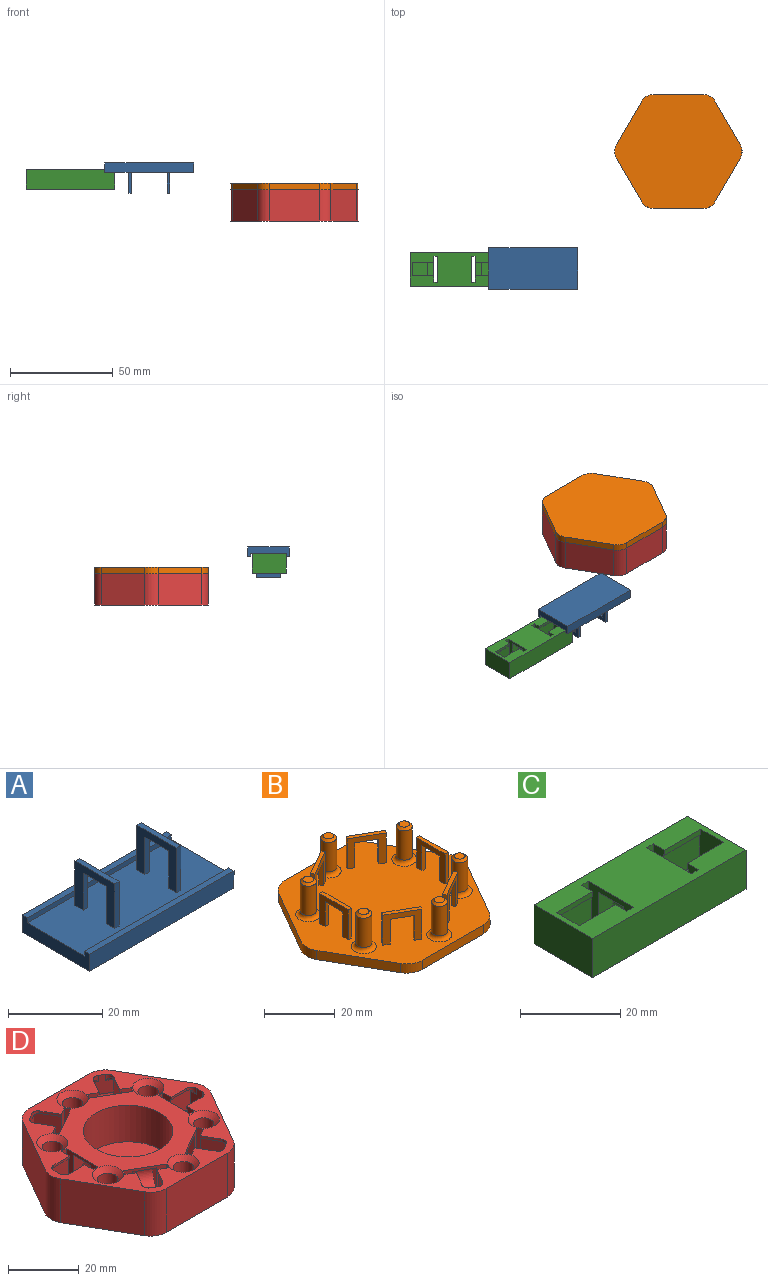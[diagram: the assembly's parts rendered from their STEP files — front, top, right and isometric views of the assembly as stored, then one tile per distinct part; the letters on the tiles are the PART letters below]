
ASSEMBLY  parts=4 mates=3
PART A: 26 faces, bbox 43.2x20.3x14.7 mm
  f0: plane 43.18x17.27mm, normal (0,0,1), area 733.5mm2, adj f1,f5,f8,f9,f10,f12,f13,f15
  f1: plane 20.32x4.45mm, normal (-1,0,0), area 68.4mm2, adj f0,f2,f3,f4,f5,f6,f7,f8
  f2: plane 43.18x4.45mm, normal (0,-1,0), area 191.9mm2, adj f1,f4,f6,f17
  f3: plane 43.18x4.45mm, normal (0,1,0), area 191.9mm2, adj f1,f4,f7,f17
  f4: plane 43.18x20.32mm, normal (0,0,-1), area 877.4mm2, adj f1,f2,f3,f17
  f5: plane 43.18x1.27mm, normal (0,1,0), area 54.8mm2, adj f0,f1,f6,f17
  f6: plane 43.18x1.52mm, normal (0,0,1), area 65.8mm2, adj f1,f2,f5,f17
  f7: plane 43.18x1.52mm, normal (0,0,1), area 65.8mm2, adj f1,f3,f8,f17
  f8: plane 43.18x1.27mm, normal (0,-1,0), area 54.8mm2, adj f0,f1,f7,f17
  f9: plane 11.56x1.27mm, normal (0,-1,0), area 14.7mm2, adj f0,f14,f15,f16
  f10: plane 9.65x1.27mm, normal (0,1,0), area 12.3mm2, adj f0,f11,f15,f16
  f11: plane 7.11x1.27mm, normal (0,0,-1), area 9mm2, adj f10,f12,f15,f16
  f12: plane 9.65x1.27mm, normal (0,-1,0), area 12.3mm2, adj f0,f11,f15,f16
  f13: plane 11.56x1.27mm, normal (0,1,0), area 14.7mm2, adj f0,f14,f15,f16
  f14: plane 11.94x1.27mm, normal (0,0,1), area 15.2mm2, adj f9,f13,f15,f16
  f15: plane 11.94x11.56mm, normal (-1,0,0), area 69.3mm2, adj f0,f9,f10,f11,f12,f13,f14
  f16: plane 11.94x11.56mm, normal (1,0,0), area 69.3mm2, adj f0,f9,f10,f11,f12,f13,f14
  f17: plane 20.32x4.45mm, normal (1,0,0), area 68.4mm2, adj f0,f2,f3,f4,f5,f6,f7,f8
  f18: plane 11.56x1.27mm, normal (0,-1,0), area 14.7mm2, adj f0,f23,f24,f25
  f19: plane 9.65x1.27mm, normal (0,1,0), area 12.3mm2, adj f0,f20,f24,f25
  f20: plane 7.11x1.27mm, normal (0,0,-1), area 9mm2, adj f19,f21,f24,f25
  f21: plane 9.65x1.27mm, normal (0,-1,0), area 12.3mm2, adj f0,f20,f24,f25
  f22: plane 11.56x1.27mm, normal (0,1,0), area 14.7mm2, adj f0,f23,f24,f25
  f23: plane 11.94x1.27mm, normal (0,0,1), area 15.2mm2, adj f18,f22,f24,f25
  f24: plane 11.94x11.56mm, normal (1,0,0), area 69.3mm2, adj f0,f18,f19,f20,f21,f22,f23
  f25: plane 11.94x11.56mm, normal (-1,0,0), area 69.3mm2, adj f0,f18,f19,f20,f21,f22,f23
PART B: 86 faces, bbox 61.8x55.2x15.4 mm
  f0: plane 21.27x12.28mm, normal (0.87,-0.5,0), area 78mm2, adj f6,f7,f80,f85
  f1: plane 21.27x12.28mm, normal (0.87,0.5,0), area 78mm2, adj f6,f7,f80,f81
  f2: plane 24.56x3.18mm, normal (0,1,0), area 78mm2, adj f6,f7,f81,f82
  f3: plane 21.27x12.28mm, normal (-0.87,0.5,0), area 78mm2, adj f6,f7,f82,f83
  f4: plane 21.27x12.28mm, normal (-0.87,-0.5,0), area 78mm2, adj f6,f7,f83,f84
  f5: plane 24.56x3.18mm, normal (0,-1,0), area 78mm2, adj f6,f7,f84,f85
  f6: plane 61.83x55.25mm, normal (0,0,1), area 2358.9mm2, adj f0,f1,f2,f3,f4,f5,f8,f10
  f7: plane 61.83x55.25mm, normal (0,0,-1), area 2630.1mm2, adj f0,f1,f2,f3,f4,f5,f80,f81
  f8: plane 10.41x1.27mm, normal (0,1,0), area 13.2mm2, adj f6,f9,f14,f15
  f9: plane 11.43x1.27mm, normal (0,0,1), area 14.5mm2, adj f8,f10,f14,f15
  f10: plane 10.41x1.27mm, normal (0,-1,0), area 13.2mm2, adj f6,f9,f14,f15
  f11: plane 8.64x1.27mm, normal (0,1,0), area 11mm2, adj f6,f12,f14,f15
  f12: plane 7.11x1.27mm, normal (0,0,-1), area 9mm2, adj f11,f13,f14,f15
  f13: plane 8.64x1.27mm, normal (0,-1,0), area 11mm2, adj f6,f12,f14,f15
  f14: plane 11.43x10.41mm, normal (1,0,0), area 57.6mm2, adj f6,f8,f9,f10,f11,f12,f13
  f15: plane 11.43x10.41mm, normal (-1,0,0), area 57.6mm2, adj f6,f8,f9,f10,f11,f12,f13
  f16: cylinder r=2.29mm len=10.16mm, axis (0,0,-1), area 145.9mm2, adj f18,f19
  f17: plane 3.05x3.05mm, normal (0,0,1), area 7.3mm2, adj f18
  f18: cone r=1.52mm half-angle=45deg, axis (0,0,-1), area 12.9mm2, adj f16,f17
  f19: torus R=3.56mm, axis (0,0,1), area 34.4mm2, adj f6,f16
  f20: plane 10.41x1.1mm, normal (-0.87,0.5,0), area 13.2mm2, adj f6,f21,f26,f27
  f21: plane 10.53x6.82mm, normal (0,0,1), area 14.5mm2, adj f20,f22,f26,f27
  f22: plane 10.41x1.1mm, normal (0.87,-0.5,0), area 13.2mm2, adj f6,f21,f26,f27
  f23: plane 8.64x1.1mm, normal (-0.87,0.5,0), area 11mm2, adj f6,f24,f26,f27
  f24: plane 6.79x4.66mm, normal (0,0,-1), area 9mm2, adj f23,f25,f26,f27
  f25: plane 8.64x1.1mm, normal (0.87,-0.5,0), area 11mm2, adj f6,f24,f26,f27
  f26: plane 10.41x9.9mm, normal (0.5,0.87,0), area 57.6mm2, adj f6,f20,f21,f22,f23,f24,f25
  f27: plane 10.41x9.9mm, normal (-0.5,-0.87,0), area 57.6mm2, adj f6,f20,f21,f22,f23,f24,f25
  f28: cylinder r=2.29mm len=10.16mm, axis (0,0,-1), area 145.9mm2, adj f30,f31
  f29: plane 3.05x3.05mm, normal (0,0,1), area 7.3mm2, adj f30
  f30: cone r=1.52mm half-angle=45deg, axis (0,0,-1), area 12.9mm2, adj f28,f29
  f31: torus R=3.56mm, axis (0,0,1), area 34.4mm2, adj f6,f28
  f32: plane 10.41x1.1mm, normal (-0.87,-0.5,0), area 13.2mm2, adj f6,f33,f38,f39
  f33: plane 10.53x6.82mm, normal (0,0,1), area 14.5mm2, adj f32,f34,f38,f39
  f34: plane 10.41x1.1mm, normal (0.87,0.5,0), area 13.2mm2, adj f6,f33,f38,f39
  f35: plane 8.64x1.1mm, normal (-0.87,-0.5,0), area 11mm2, adj f6,f36,f38,f39
  f36: plane 6.79x4.66mm, normal (0,0,-1), area 9mm2, adj f35,f37,f38,f39
  f37: plane 8.64x1.1mm, normal (0.87,0.5,0), area 11mm2, adj f6,f36,f38,f39
  f38: plane 10.41x9.9mm, normal (-0.5,0.87,0), area 57.6mm2, adj f6,f32,f33,f34,f35,f36,f37
  f39: plane 10.41x9.9mm, normal (0.5,-0.87,0), area 57.6mm2, adj f6,f32,f33,f34,f35,f36,f37
  f40: cylinder r=2.29mm len=10.16mm, axis (0,0,-1), area 145.9mm2, adj f42,f43
  f41: plane 3.05x3.05mm, normal (0,0,1), area 7.3mm2, adj f42
  f42: cone r=1.52mm half-angle=45deg, axis (0,0,-1), area 12.9mm2, adj f40,f41
  f43: torus R=3.56mm, axis (0,0,1), area 34.4mm2, adj f6,f40
  f44: plane 10.41x1.27mm, normal (0,-1,0), area 13.2mm2, adj f6,f45,f50,f51
  f45: plane 11.43x1.27mm, normal (0,0,1), area 14.5mm2, adj f44,f46,f50,f51
  f46: plane 10.41x1.27mm, normal (0,1,0), area 13.2mm2, adj f6,f45,f50,f51
  f47: plane 8.64x1.27mm, normal (0,-1,0), area 11mm2, adj f6,f48,f50,f51
  f48: plane 7.11x1.27mm, normal (0,0,-1), area 9mm2, adj f47,f49,f50,f51
  f49: plane 8.64x1.27mm, normal (0,1,0), area 11mm2, adj f6,f48,f50,f51
  f50: plane 11.43x10.41mm, normal (-1,0,0), area 57.6mm2, adj f6,f44,f45,f46,f47,f48,f49
  f51: plane 11.43x10.41mm, normal (1,0,0), area 57.6mm2, adj f6,f44,f45,f46,f47,f48,f49
  f52: cylinder r=2.29mm len=10.16mm, axis (0,0,-1), area 145.9mm2, adj f54,f55
  f53: plane 3.05x3.05mm, normal (0,0,1), area 7.3mm2, adj f54
  f54: cone r=1.52mm half-angle=45deg, axis (0,0,-1), area 12.9mm2, adj f52,f53
  f55: torus R=3.56mm, axis (0,0,1), area 34.4mm2, adj f6,f52
  f56: plane 10.41x1.1mm, normal (0.87,-0.5,0), area 13.2mm2, adj f6,f57,f62,f63
  f57: plane 10.53x6.82mm, normal (0,0,1), area 14.5mm2, adj f56,f58,f62,f63
  f58: plane 10.41x1.1mm, normal (-0.87,0.5,0), area 13.2mm2, adj f6,f57,f62,f63
  f59: plane 8.64x1.1mm, normal (0.87,-0.5,0), area 11mm2, adj f6,f60,f62,f63
  f60: plane 6.79x4.66mm, normal (0,0,-1), area 9mm2, adj f59,f61,f62,f63
  f61: plane 8.64x1.1mm, normal (-0.87,0.5,0), area 11mm2, adj f6,f60,f62,f63
  f62: plane 10.41x9.9mm, normal (-0.5,-0.87,0), area 57.6mm2, adj f6,f56,f57,f58,f59,f60,f61
  f63: plane 10.41x9.9mm, normal (0.5,0.87,0), area 57.6mm2, adj f6,f56,f57,f58,f59,f60,f61
  f64: cylinder r=2.29mm len=10.16mm, axis (0,0,-1), area 145.9mm2, adj f66,f67
  f65: plane 3.05x3.05mm, normal (0,0,1), area 7.3mm2, adj f66
  f66: cone r=1.52mm half-angle=45deg, axis (0,0,-1), area 12.9mm2, adj f64,f65
  f67: torus R=3.56mm, axis (0,0,1), area 34.4mm2, adj f6,f64
  f68: plane 10.41x1.1mm, normal (0.87,0.5,0), area 13.2mm2, adj f6,f69,f74,f75
  f69: plane 10.53x6.82mm, normal (0,0,1), area 14.5mm2, adj f68,f70,f74,f75
  f70: plane 10.41x1.1mm, normal (-0.87,-0.5,0), area 13.2mm2, adj f6,f69,f74,f75
  f71: plane 8.64x1.1mm, normal (0.87,0.5,0), area 11mm2, adj f6,f72,f74,f75
  f72: plane 6.79x4.66mm, normal (0,0,-1), area 9mm2, adj f71,f73,f74,f75
  f73: plane 8.64x1.1mm, normal (-0.87,-0.5,0), area 11mm2, adj f6,f72,f74,f75
  f74: plane 10.41x9.9mm, normal (0.5,-0.87,0), area 57.6mm2, adj f6,f68,f69,f70,f71,f72,f73
  f75: plane 10.41x9.9mm, normal (-0.5,0.87,0), area 57.6mm2, adj f6,f68,f69,f70,f71,f72,f73
  f76: cylinder r=2.29mm len=10.16mm, axis (0,0,-1), area 145.9mm2, adj f78,f79
  f77: plane 3.05x3.05mm, normal (0,0,1), area 7.3mm2, adj f78
  f78: cone r=1.52mm half-angle=45deg, axis (0,0,-1), area 12.9mm2, adj f76,f77
  f79: torus R=3.56mm, axis (0,0,1), area 34.4mm2, adj f6,f76
  f80: cylinder r=6.35mm len=6.35mm, axis (0,0,-1), area 21.1mm2, adj f0,f1,f6,f7
  f81: cylinder r=6.35mm len=5.5mm, axis (0,0,-1), area 21.1mm2, adj f1,f2,f6,f7
  f82: cylinder r=6.35mm len=5.5mm, axis (0,0,-1), area 21.1mm2, adj f2,f3,f6,f7
  f83: cylinder r=6.35mm len=6.35mm, axis (0,0,-1), area 21.1mm2, adj f3,f4,f6,f7
  f84: cylinder r=6.35mm len=5.5mm, axis (0,0,-1), area 21.1mm2, adj f4,f5,f6,f7
  f85: cylinder r=6.35mm len=5.5mm, axis (0,0,-1), area 21.1mm2, adj f0,f5,f6,f7
PART C: 52 faces, bbox 43.2x16.5x9.5 mm
  f0: plane 6.99x0.38mm, normal (0.02,0,-1), area 2.7mm2, adj f1,f6,f13,f26
  f1: cylinder r=10.16mm len=0.53mm, axis (0,1,0), area 0.2mm2, adj f0,f2,f13,f26
  f2: plane 2.74x0.38mm, normal (-0.03,0,-1), area 1mm2, adj f1,f3,f13,f26
  f3: plane 12.7x9.53mm, normal (1,0,0), area 63.3mm2, adj f2,f4,f9,f10,f12,f13,f14,f15
  f4: plane 43.18x16.51mm, normal (0,0,1), area 534.2mm2, adj f3,f6,f14,f15,f16,f18,f19,f20
  f5: plane 7.11x7.11mm, normal (-0.02,0,1), area 50.6mm2, adj f6,f11,f12,f13
  f6: plane 8.26x7.11mm, normal (1,0,0), area 57.7mm2, adj f0,f4,f5,f7,f12,f13,f26,f27
  f7: plane 6.99x0.38mm, normal (0.02,0,-1), area 2.7mm2, adj f6,f8,f12,f27
  f8: cylinder r=10.16mm len=0.53mm, axis (0,1,0), area 0.2mm2, adj f7,f9,f12,f27
  f9: plane 2.74x0.38mm, normal (-0.03,0,-1), area 1mm2, adj f3,f8,f12,f27
  f10: plane 7.11x2.98mm, normal (0.03,0,1), area 21.2mm2, adj f3,f11,f12,f13
  f11: cylinder r=3.17mm len=7.11mm, axis (0,1,0), area 1.2mm2, adj f5,f10,f12,f13
  f12: plane 10.26x7.11mm, normal (0,1,0), area 71.7mm2, adj f3,f5,f6,f7,f8,f9,f10,f11
  f13: plane 10.26x7.11mm, normal (0,-1,0), area 71.7mm2, adj f0,f1,f2,f3,f5,f6,f10,f11
  f14: plane 9.53x1.91mm, normal (0,-1,0), area 18.1mm2, adj f3,f4,f16,f17
  f15: plane 9.53x1.91mm, normal (0,1,0), area 18.1mm2, adj f3,f4,f16,f17
  f16: plane 12.7x9.53mm, normal (-1,0,0), area 71.3mm2, adj f4,f14,f15,f17,f22,f23,f24,f25
  f17: plane 43.18x16.51mm, normal (0,0,-1), area 664.5mm2, adj f3,f14,f15,f16,f18,f19,f20,f31
  f18: plane 16.51x9.53mm, normal (-1,0,0), area 157.3mm2, adj f4,f17,f19,f20
  f19: plane 43.18x9.53mm, normal (0,-1,0), area 411.3mm2, adj f4,f17,f18,f44
  f20: plane 43.18x9.53mm, normal (0,1,0), area 411.3mm2, adj f4,f17,f18,f44
  f21: cylinder r=3.49mm len=7.11mm, axis (0,1,0), area 78mm2, adj f22,f23,f24,f25
  f22: plane 7.02x4.32mm, normal (0,1,0), area 24.9mm2, adj f16,f21,f24,f25
  f23: plane 7.02x4.32mm, normal (0,-1,0), area 24.9mm2, adj f16,f21,f24,f25
  f24: plane 7.11x0.71mm, normal (0.03,0,1), area 5mm2, adj f16,f21,f22,f23
  f25: plane 7.11x0.95mm, normal (-0.03,0,-1), area 6.8mm2, adj f16,f21,f22,f23
  f26: plane 10.26x1.27mm, normal (0,-1,0), area 12.3mm2, adj f0,f1,f2,f3,f4,f6
  f27: plane 10.26x1.27mm, normal (0,1,0), area 12.3mm2, adj f3,f4,f6,f7,f8,f9
  f28: plane 6.99x0.38mm, normal (-0.02,0,-1), area 2.7mm2, adj f29,f33,f40,f50
  f29: cylinder r=10.16mm len=0.53mm, axis (0,1,0), area 0.2mm2, adj f28,f30,f40,f50
  f30: plane 2.74x0.38mm, normal (0.03,0,-1), area 1mm2, adj f29,f31,f40,f50
  f31: plane 12.7x9.53mm, normal (-1,0,0), area 63.3mm2, adj f4,f17,f30,f36,f37,f39,f40,f41
  f32: plane 7.11x7.11mm, normal (0.02,0,1), area 50.6mm2, adj f33,f38,f39,f40
  f33: plane 8.26x7.11mm, normal (-1,0,0), area 57.7mm2, adj f4,f28,f32,f34,f39,f40,f50,f51
  f34: plane 6.99x0.38mm, normal (-0.02,0,-1), area 2.7mm2, adj f33,f35,f39,f51
  f35: cylinder r=10.16mm len=0.53mm, axis (0,1,0), area 0.2mm2, adj f34,f36,f39,f51
  f36: plane 2.74x0.38mm, normal (0.03,0,-1), area 1mm2, adj f31,f35,f39,f51
  f37: plane 7.11x2.98mm, normal (-0.03,0,1), area 21.2mm2, adj f31,f38,f39,f40
  f38: cylinder r=3.17mm len=7.11mm, axis (0,1,0), area 1.2mm2, adj f32,f37,f39,f40
  f39: plane 10.26x7.11mm, normal (0,1,0), area 71.7mm2, adj f31,f32,f33,f34,f35,f36,f37,f38
  f40: plane 10.26x7.11mm, normal (0,-1,0), area 71.7mm2, adj f28,f29,f30,f31,f32,f33,f37,f38
  f41: plane 9.53x1.91mm, normal (0,-1,0), area 18.1mm2, adj f4,f17,f31,f43
  f42: plane 9.53x1.91mm, normal (0,1,0), area 18.1mm2, adj f4,f17,f31,f43
  f43: plane 12.7x9.53mm, normal (1,0,0), area 71.3mm2, adj f4,f17,f41,f42,f46,f47,f48,f49
  f44: plane 16.51x9.53mm, normal (1,0,0), area 157.3mm2, adj f4,f17,f19,f20
  f45: cylinder r=3.49mm len=7.11mm, axis (0,1,0), area 78mm2, adj f46,f47,f48,f49
  f46: plane 7.02x4.32mm, normal (0,1,0), area 24.9mm2, adj f43,f45,f48,f49
  f47: plane 7.02x4.32mm, normal (0,-1,0), area 24.9mm2, adj f43,f45,f48,f49
  f48: plane 7.11x0.71mm, normal (-0.03,0,1), area 5mm2, adj f43,f45,f46,f47
  f49: plane 7.11x0.95mm, normal (0.03,0,-1), area 6.8mm2, adj f43,f45,f46,f47
  f50: plane 10.26x1.27mm, normal (0,-1,0), area 12.3mm2, adj f4,f28,f29,f30,f31,f33
  f51: plane 10.26x1.27mm, normal (0,1,0), area 12.3mm2, adj f4,f31,f33,f34,f35,f36
PART D: 196 faces, bbox 61.8x55.2x15.2 mm
  f0: plane 61.83x55.25mm, normal (0,0,1), area 1314.2mm2, adj f1,f5,f9,f13,f17,f24,f32,f35
  f1: plane 11x10.92mm, normal (0.5,0.87,0), area 85mm2, adj f0,f2,f159,f161,f162,f163,f164,f165
  f2: plane 1.85x1.32mm, normal (-0.01,-0.02,-1), area 0.8mm2, adj f1,f3,f165,f178
  f3: plane 4.71x2.94mm, normal (0.01,0.02,-1), area 2.3mm2, adj f2,f4,f165,f178,f180
  f4: cylinder r=1.27mm len=2.65mm, axis (0.87,-0.5,0), area 2.6mm2, adj f3,f165,f170,f180
  f5: plane 11x10.92mm, normal (-0.5,0.87,0), area 85mm2, adj f0,f6,f134,f136,f137,f138,f139,f140
  f6: plane 1.85x1.32mm, normal (0.01,-0.02,-1), area 0.8mm2, adj f5,f7,f140,f153
  f7: plane 4.65x3.05mm, normal (-0.01,0.02,-1), area 2.3mm2, adj f6,f8,f140,f153,f155
  f8: cylinder r=1.27mm len=2.65mm, axis (0.87,0.5,0), area 2.6mm2, adj f7,f140,f145,f155
  f9: plane 12.7x10.92mm, normal (-1,0,0), area 85mm2, adj f0,f10,f109,f111,f112,f113,f114,f115
  f10: plane 1.88x0.44mm, normal (0.03,0,-1), area 0.8mm2, adj f9,f11,f115,f128
  f11: plane 5.11x0.57mm, normal (-0.03,0,-1), area 2.3mm2, adj f10,f12,f115,f128,f130
  f12: cylinder r=1.27mm len=2.35mm, axis (0,1,0), area 2.6mm2, adj f11,f115,f120,f130
  f13: plane 11x10.92mm, normal (-0.5,-0.87,0), area 85mm2, adj f0,f14,f84,f86,f87,f88,f89,f90
  f14: plane 1.85x1.32mm, normal (0.01,0.02,-1), area 0.8mm2, adj f13,f15,f90,f103
  f15: plane 4.71x2.94mm, normal (-0.01,-0.02,-1), area 2.3mm2, adj f14,f16,f90,f103,f105
  f16: cylinder r=1.27mm len=2.65mm, axis (-0.87,0.5,0), area 2.6mm2, adj f15,f90,f95,f105
  f17: plane 11x10.92mm, normal (0.5,-0.87,0), area 85mm2, adj f0,f18,f59,f61,f62,f63,f64,f65
  f18: plane 1.85x1.32mm, normal (-0.01,0.02,-1), area 0.8mm2, adj f17,f19,f65,f78
  f19: plane 4.65x3.05mm, normal (0.01,-0.02,-1), area 2.3mm2, adj f18,f20,f65,f78,f80
  f20: cylinder r=1.27mm len=2.65mm, axis (-0.87,-0.5,0), area 2.6mm2, adj f19,f65,f70,f80
  f21: plane 1.88x0.44mm, normal (-0.03,0,-1), area 0.8mm2, adj f22,f24,f27,f53
  f22: plane 5.11x0.57mm, normal (0.03,0,-1), area 2.3mm2, adj f21,f23,f27,f53,f55
  f23: cylinder r=1.27mm len=2.35mm, axis (0,-1,0), area 2.6mm2, adj f22,f27,f32,f55
  f24: plane 12.7x10.92mm, normal (1,0,0), area 85mm2, adj f0,f21,f25,f26,f27,f28,f35,f37
  f25: plane 6.99x1.71mm, normal (0.03,0,1), area 12mm2, adj f24,f27,f28,f29
  f26: plane 1.88x0.44mm, normal (-0.03,0,-1), area 0.8mm2, adj f24,f28,f30,f54
  f27: plane 8.23x7.12mm, normal (0,-1,0), area 56.8mm2, adj f21,f22,f23,f24,f25,f29,f32,f33
  f28: plane 8.23x7.12mm, normal (0,1,0), area 56.8mm2, adj f24,f25,f26,f29,f30,f31,f32,f33
  f29: cylinder r=3.17mm len=6.99mm, axis (0,-1,0), area 1.2mm2, adj f25,f27,f28,f34
  f30: plane 5.11x0.57mm, normal (0.03,0,-1), area 2.3mm2, adj f26,f28,f31,f54,f56
  f31: cylinder r=1.27mm len=2.35mm, axis (0,-1,0), area 2.6mm2, adj f28,f30,f32,f56
  f32: plane 6.99x6.62mm, normal (1,0,0), area 36mm2, adj f0,f23,f27,f28,f31,f33,f55,f56
  f33: cylinder r=1.27mm len=6.99mm, axis (0,-1,0), area 14.2mm2, adj f27,f28,f32,f34
  f34: plane 6.99x5.05mm, normal (-0.03,0,1), area 35.3mm2, adj f27,f28,f29,f33
  f35: plane 10.92x1.91mm, normal (0,1,0), area 20.8mm2, adj f0,f24,f36,f38
  f36: plane 12.7x10.92mm, normal (-1,0,0), area 89.9mm2, adj f0,f35,f37,f38,f49,f50,f51,f52
  f37: plane 10.92x1.91mm, normal (0,-1,0), area 20.8mm2, adj f0,f24,f36,f38
  f38: plane 12.7x1.91mm, normal (0,0,1), area 24.2mm2, adj f24,f35,f36,f37
  f39: plane 21.27x15.24mm, normal (-0.87,-0.5,0), area 374.3mm2, adj f0,f45,f184,f189
  f40: plane 24.56x15.24mm, normal (0,-1,0), area 374.3mm2, adj f0,f45,f184,f185
  f41: plane 21.27x15.24mm, normal (0.87,-0.5,0), area 374.3mm2, adj f0,f45,f185,f186
  f42: plane 21.27x15.24mm, normal (0.87,0.5,0), area 374.3mm2, adj f0,f45,f186,f187
  f43: plane 24.56x15.24mm, normal (0,1,0), area 374.3mm2, adj f0,f45,f187,f188
  f44: plane 21.27x15.24mm, normal (-0.87,0.5,0), area 374.3mm2, adj f0,f45,f188,f189
  f45: plane 61.83x55.25mm, normal (0,0,-1), area 2630.1mm2, adj f39,f40,f41,f42,f43,f44,f184,f185
  f46: cylinder r=12.7mm len=25.4mm, axis (0,0,1), area 1013.4mm2, adj f0,f47
  f47: plane 25.4x25.4mm, normal (0,0,1), area 506.7mm2, adj f46
  f48: cylinder r=3.49mm len=6.99mm, axis (0,-1,0), area 76.6mm2, adj f49,f50,f51,f52
  f49: plane 7.01x4.32mm, normal (0,-1,0), area 24.9mm2, adj f36,f48,f51,f52
  f50: plane 7.01x4.32mm, normal (0,1,0), area 24.9mm2, adj f36,f48,f51,f52
  f51: plane 6.99x0.92mm, normal (-0.03,0,-1), area 6.4mm2, adj f36,f48,f49,f50
  f52: plane 6.99x0.74mm, normal (0.03,0,1), area 5.1mm2, adj f36,f48,f49,f50
  f53: plane 6.32x0.88mm, normal (0,-1,0), area 5.1mm2, adj f0,f21,f22,f24,f55
  f54: plane 6.32x0.88mm, normal (0,1,0), area 5.1mm2, adj f0,f24,f26,f30,f56
  f55: cylinder r=1.91mm len=2.17mm, axis (0,0,1), area 3.8mm2, adj f0,f22,f23,f32,f53
  f56: cylinder r=1.91mm len=2.17mm, axis (0,0,1), area 3.8mm2, adj f0,f30,f31,f32,f54
  f57: cylinder r=2.92mm len=11.18mm, axis (0,0,1), area 205.1mm2, adj f58,f195
  f58: plane 5.84x5.84mm, normal (0,0,1), area 26.8mm2, adj f57
  f59: plane 10.92x1.65mm, normal (0.87,0.5,0), area 20.8mm2, adj f0,f17,f60,f62
  f60: plane 11x10.92mm, normal (-0.5,0.87,0), area 89.9mm2, adj f0,f59,f61,f62,f74,f75,f76,f77
  f61: plane 10.92x1.65mm, normal (-0.87,-0.5,0), area 20.8mm2, adj f0,f17,f60,f62
  f62: plane 11.95x8mm, normal (0,0,1), area 24.2mm2, adj f17,f59,f60,f61
  f63: plane 6.91x4.98mm, normal (0.01,-0.02,1), area 12mm2, adj f17,f65,f66,f67
  f64: plane 1.85x1.32mm, normal (-0.01,0.02,-1), area 0.8mm2, adj f17,f66,f68,f79
  f65: plane 7.13x7.12mm, normal (-0.87,-0.5,0), area 56.8mm2, adj f17,f18,f19,f20,f63,f67,f70,f71
  f66: plane 7.13x7.12mm, normal (0.87,0.5,0), area 56.8mm2, adj f17,f63,f64,f67,f68,f69,f70,f71
  f67: cylinder r=3.17mm len=6.13mm, axis (-0.87,-0.5,0), area 1.2mm2, adj f63,f65,f66,f72
  f68: plane 4.71x2.94mm, normal (0.01,-0.02,-1), area 2.3mm2, adj f64,f66,f69,f79,f81
  f69: cylinder r=1.27mm len=2.65mm, axis (-0.87,-0.5,0), area 2.6mm2, adj f66,f68,f70,f81
  f70: plane 6.62x6.05mm, normal (0.5,-0.87,0), area 36mm2, adj f0,f20,f65,f66,f69,f71,f80,f81
  f71: cylinder r=1.27mm len=6.7mm, axis (-0.87,-0.5,0), area 14.2mm2, adj f65,f66,f70,f72
  f72: plane 8.57x7.86mm, normal (-0.01,0.02,1), area 35.3mm2, adj f65,f66,f67,f71
  f73: cylinder r=3.49mm len=7.84mm, axis (-0.87,-0.5,0), area 76.6mm2, adj f74,f75,f76,f77
  f74: plane 7.01x3.74mm, normal (-0.87,-0.5,0), area 24.9mm2, adj f60,f73,f76,f77
  f75: plane 7.01x3.74mm, normal (0.87,0.5,0), area 24.9mm2, adj f60,f73,f76,f77
  f76: plane 6.51x4.29mm, normal (-0.01,0.02,-1), area 6.4mm2, adj f60,f73,f74,f75
  f77: plane 6.42x4.13mm, normal (0.01,-0.02,1), area 5.1mm2, adj f60,f73,f74,f75
  f78: plane 5.48x3.16mm, normal (-0.87,-0.5,0), area 5.1mm2, adj f0,f17,f18,f19,f80
  f79: plane 5.48x3.16mm, normal (0.87,0.5,0), area 5.1mm2, adj f0,f17,f64,f68,f81
  f80: cylinder r=1.91mm len=2.6mm, axis (0,0,1), area 3.8mm2, adj f0,f19,f20,f70,f78
  f81: cylinder r=1.91mm len=2.6mm, axis (0,0,1), area 3.8mm2, adj f0,f68,f69,f70,f79
  f82: cylinder r=2.92mm len=11.18mm, axis (0,0,1), area 205.1mm2, adj f83,f194
  f83: plane 5.84x5.84mm, normal (0,0,1), area 26.8mm2, adj f82
  f84: plane 10.92x1.65mm, normal (0.87,-0.5,0), area 20.8mm2, adj f0,f13,f85,f87
  f85: plane 11x10.92mm, normal (0.5,0.87,0), area 89.9mm2, adj f0,f84,f86,f87,f99,f100,f101,f102
  f86: plane 10.92x1.65mm, normal (-0.87,0.5,0), area 20.8mm2, adj f0,f13,f85,f87
  f87: plane 11.95x8mm, normal (0,0,1), area 24.2mm2, adj f13,f84,f85,f86
  f88: plane 6.91x4.98mm, normal (-0.01,-0.02,1), area 12mm2, adj f13,f90,f91,f92
  f89: plane 1.85x1.32mm, normal (0.01,0.02,-1), area 0.8mm2, adj f13,f91,f93,f104
  f90: plane 7.13x7.12mm, normal (-0.87,0.5,0), area 56.8mm2, adj f13,f14,f15,f16,f88,f92,f95,f96
  f91: plane 7.13x7.12mm, normal (0.87,-0.5,0), area 56.8mm2, adj f13,f88,f89,f92,f93,f94,f95,f96
  f92: cylinder r=3.17mm len=6.13mm, axis (-0.87,0.5,0), area 1.2mm2, adj f88,f90,f91,f97
  f93: plane 4.65x3.05mm, normal (-0.01,-0.02,-1), area 2.3mm2, adj f89,f91,f94,f104,f106
  f94: cylinder r=1.27mm len=2.65mm, axis (-0.87,0.5,0), area 2.6mm2, adj f91,f93,f95,f106
  f95: plane 6.62x6.05mm, normal (-0.5,-0.87,0), area 36mm2, adj f0,f16,f90,f91,f94,f96,f105,f106
  f96: cylinder r=1.27mm len=6.7mm, axis (-0.87,0.5,0), area 14.2mm2, adj f90,f91,f95,f97
  f97: plane 8.57x7.86mm, normal (0.01,0.02,1), area 35.3mm2, adj f90,f91,f92,f96
  f98: cylinder r=3.49mm len=7.84mm, axis (-0.87,0.5,0), area 76.6mm2, adj f99,f100,f101,f102
  f99: plane 7.01x3.74mm, normal (-0.87,0.5,0), area 24.9mm2, adj f85,f98,f101,f102
  f100: plane 7.01x3.74mm, normal (0.87,-0.5,0), area 24.9mm2, adj f85,f98,f101,f102
  f101: plane 6.51x4.29mm, normal (0.01,0.02,-1), area 6.4mm2, adj f85,f98,f99,f100
  f102: plane 6.42x4.13mm, normal (-0.01,-0.02,1), area 5.1mm2, adj f85,f98,f99,f100
  f103: plane 5.48x3.16mm, normal (-0.87,0.5,0), area 5.1mm2, adj f0,f13,f14,f15,f105
  f104: plane 5.48x3.16mm, normal (0.87,-0.5,0), area 5.1mm2, adj f0,f13,f89,f93,f106
  f105: cylinder r=1.91mm len=2.6mm, axis (0,0,1), area 3.8mm2, adj f0,f15,f16,f95,f103
  f106: cylinder r=1.91mm len=2.6mm, axis (0,0,1), area 3.8mm2, adj f0,f93,f94,f95,f104
  f107: cylinder r=2.92mm len=11.18mm, axis (0,0,1), area 205.1mm2, adj f108,f193
  f108: plane 5.84x5.84mm, normal (0,0,1), area 26.8mm2, adj f107
  f109: plane 10.92x1.91mm, normal (0,-1,0), area 20.8mm2, adj f0,f9,f110,f112
  f110: plane 12.7x10.92mm, normal (1,0,0), area 89.9mm2, adj f0,f109,f111,f112,f124,f125,f126,f127
  f111: plane 10.92x1.91mm, normal (0,1,0), area 20.8mm2, adj f0,f9,f110,f112
  f112: plane 12.7x1.91mm, normal (0,0,1), area 24.2mm2, adj f9,f109,f110,f111
  f113: plane 6.99x1.71mm, normal (-0.03,0,1), area 12mm2, adj f9,f115,f116,f117
  f114: plane 1.88x0.44mm, normal (0.03,0,-1), area 0.8mm2, adj f9,f116,f118,f129
  f115: plane 8.23x7.12mm, normal (0,1,0), area 56.8mm2, adj f9,f10,f11,f12,f113,f117,f120,f121
  f116: plane 8.23x7.12mm, normal (0,-1,0), area 56.8mm2, adj f9,f113,f114,f117,f118,f119,f120,f121
  f117: cylinder r=3.17mm len=6.99mm, axis (0,1,0), area 1.2mm2, adj f113,f115,f116,f122
  f118: plane 5.11x0.57mm, normal (-0.03,0,-1), area 2.3mm2, adj f114,f116,f119,f129,f131
  f119: cylinder r=1.27mm len=2.35mm, axis (0,1,0), area 2.6mm2, adj f116,f118,f120,f131
  f120: plane 6.99x6.62mm, normal (-1,0,0), area 36mm2, adj f0,f12,f115,f116,f119,f121,f130,f131
  f121: cylinder r=1.27mm len=6.99mm, axis (0,1,0), area 14.2mm2, adj f115,f116,f120,f122
  f122: plane 6.99x5.05mm, normal (0.03,0,1), area 35.3mm2, adj f115,f116,f117,f121
  f123: cylinder r=3.49mm len=6.99mm, axis (0,1,0), area 76.6mm2, adj f124,f125,f126,f127
  f124: plane 7.01x4.32mm, normal (0,1,0), area 24.9mm2, adj f110,f123,f126,f127
  f125: plane 7.01x4.32mm, normal (0,-1,0), area 24.9mm2, adj f110,f123,f126,f127
  f126: plane 6.99x0.92mm, normal (0.03,0,-1), area 6.4mm2, adj f110,f123,f124,f125
  f127: plane 6.99x0.74mm, normal (-0.03,0,1), area 5.1mm2, adj f110,f123,f124,f125
  f128: plane 6.32x0.88mm, normal (0,1,0), area 5.1mm2, adj f0,f9,f10,f11,f130
  f129: plane 6.32x0.88mm, normal (0,-1,0), area 5.1mm2, adj f0,f9,f114,f118,f131
  f130: cylinder r=1.91mm len=2.17mm, axis (0,0,1), area 3.8mm2, adj f0,f11,f12,f120,f128
  f131: cylinder r=1.91mm len=2.17mm, axis (0,0,1), area 3.8mm2, adj f0,f118,f119,f120,f129
  f132: cylinder r=2.92mm len=11.18mm, axis (0,0,1), area 205.1mm2, adj f133,f192
  f133: plane 5.84x5.84mm, normal (0,0,1), area 26.8mm2, adj f132
  f134: plane 10.92x1.65mm, normal (-0.87,-0.5,0), area 20.8mm2, adj f0,f5,f135,f137
  f135: plane 11x10.92mm, normal (0.5,-0.87,0), area 89.9mm2, adj f0,f134,f136,f137,f149,f150,f151,f152
  f136: plane 10.92x1.65mm, normal (0.87,0.5,0), area 20.8mm2, adj f0,f5,f135,f137
  f137: plane 11.95x8mm, normal (0,0,1), area 24.2mm2, adj f5,f134,f135,f136
  f138: plane 6.91x4.98mm, normal (-0.01,0.02,1), area 12mm2, adj f5,f140,f141,f142
  f139: plane 1.85x1.32mm, normal (0.01,-0.02,-1), area 0.8mm2, adj f5,f141,f143,f154
  f140: plane 7.13x7.12mm, normal (0.87,0.5,0), area 56.8mm2, adj f5,f6,f7,f8,f138,f142,f145,f146
  f141: plane 7.13x7.12mm, normal (-0.87,-0.5,0), area 56.8mm2, adj f5,f138,f139,f142,f143,f144,f145,f146
  f142: cylinder r=3.17mm len=6.13mm, axis (0.87,0.5,0), area 1.2mm2, adj f138,f140,f141,f147
  f143: plane 4.71x2.94mm, normal (-0.01,0.02,-1), area 2.3mm2, adj f139,f141,f144,f154,f156
  f144: cylinder r=1.27mm len=2.65mm, axis (0.87,0.5,0), area 2.6mm2, adj f141,f143,f145,f156
  f145: plane 6.62x6.05mm, normal (-0.5,0.87,0), area 36mm2, adj f0,f8,f140,f141,f144,f146,f155,f156
  f146: cylinder r=1.27mm len=6.7mm, axis (0.87,0.5,0), area 14.2mm2, adj f140,f141,f145,f147
  f147: plane 8.57x7.86mm, normal (0.01,-0.02,1), area 35.3mm2, adj f140,f141,f142,f146
  f148: cylinder r=3.49mm len=7.84mm, axis (0.87,0.5,0), area 76.6mm2, adj f149,f150,f151,f152
  f149: plane 7.01x3.74mm, normal (0.87,0.5,0), area 24.9mm2, adj f135,f148,f151,f152
  f150: plane 7.01x3.74mm, normal (-0.87,-0.5,0), area 24.9mm2, adj f135,f148,f151,f152
  f151: plane 6.51x4.29mm, normal (0.01,-0.02,-1), area 6.4mm2, adj f135,f148,f149,f150
  f152: plane 6.42x4.13mm, normal (-0.01,0.02,1), area 5.1mm2, adj f135,f148,f149,f150
  f153: plane 5.48x3.16mm, normal (0.87,0.5,0), area 5.1mm2, adj f0,f5,f6,f7,f155
  f154: plane 5.48x3.16mm, normal (-0.87,-0.5,0), area 5.1mm2, adj f0,f5,f139,f143,f156
  f155: cylinder r=1.91mm len=2.6mm, axis (0,0,1), area 3.8mm2, adj f0,f7,f8,f145,f153
  f156: cylinder r=1.91mm len=2.6mm, axis (0,0,1), area 3.8mm2, adj f0,f143,f144,f145,f154
  f157: cylinder r=2.92mm len=11.18mm, axis (0,0,1), area 205.1mm2, adj f158,f191
  f158: plane 5.84x5.84mm, normal (0,0,1), area 26.8mm2, adj f157
  f159: plane 10.92x1.65mm, normal (-0.87,0.5,0), area 20.8mm2, adj f0,f1,f160,f162
  f160: plane 11x10.92mm, normal (-0.5,-0.87,0), area 89.9mm2, adj f0,f159,f161,f162,f174,f175,f176,f177
  f161: plane 10.92x1.65mm, normal (0.87,-0.5,0), area 20.8mm2, adj f0,f1,f160,f162
  f162: plane 11.95x8mm, normal (0,0,1), area 24.2mm2, adj f1,f159,f160,f161
  f163: plane 6.91x4.98mm, normal (0.01,0.02,1), area 12mm2, adj f1,f165,f166,f167
  f164: plane 1.85x1.32mm, normal (-0.01,-0.02,-1), area 0.8mm2, adj f1,f166,f168,f179
  f165: plane 7.13x7.12mm, normal (0.87,-0.5,0), area 56.8mm2, adj f1,f2,f3,f4,f163,f167,f170,f171
  f166: plane 7.13x7.12mm, normal (-0.87,0.5,0), area 56.8mm2, adj f1,f163,f164,f167,f168,f169,f170,f171
  f167: cylinder r=3.17mm len=6.13mm, axis (0.87,-0.5,0), area 1.2mm2, adj f163,f165,f166,f172
  f168: plane 4.65x3.05mm, normal (0.01,0.02,-1), area 2.3mm2, adj f164,f166,f169,f179,f181
  f169: cylinder r=1.27mm len=2.65mm, axis (0.87,-0.5,0), area 2.6mm2, adj f166,f168,f170,f181
  f170: plane 6.62x6.05mm, normal (0.5,0.87,0), area 36mm2, adj f0,f4,f165,f166,f169,f171,f180,f181
  f171: cylinder r=1.27mm len=6.7mm, axis (0.87,-0.5,0), area 14.2mm2, adj f165,f166,f170,f172
  f172: plane 8.57x7.86mm, normal (-0.01,-0.02,1), area 35.3mm2, adj f165,f166,f167,f171
  f173: cylinder r=3.49mm len=7.84mm, axis (0.87,-0.5,0), area 76.6mm2, adj f174,f175,f176,f177
  f174: plane 7.01x3.74mm, normal (0.87,-0.5,0), area 24.9mm2, adj f160,f173,f176,f177
  f175: plane 7.01x3.74mm, normal (-0.87,0.5,0), area 24.9mm2, adj f160,f173,f176,f177
  f176: plane 6.51x4.29mm, normal (-0.01,-0.02,-1), area 6.4mm2, adj f160,f173,f174,f175
  f177: plane 6.42x4.13mm, normal (0.01,0.02,1), area 5.1mm2, adj f160,f173,f174,f175
  f178: plane 5.48x3.16mm, normal (0.87,-0.5,0), area 5.1mm2, adj f0,f1,f2,f3,f180
  f179: plane 5.48x3.16mm, normal (-0.87,0.5,0), area 5.1mm2, adj f0,f1,f164,f168,f181
  f180: cylinder r=1.91mm len=2.6mm, axis (0,0,1), area 3.8mm2, adj f0,f3,f4,f170,f178
  f181: cylinder r=1.91mm len=2.6mm, axis (0,0,1), area 3.8mm2, adj f0,f168,f169,f170,f179
  f182: cylinder r=2.92mm len=11.18mm, axis (0,0,1), area 205.1mm2, adj f183,f190
  f183: plane 5.84x5.84mm, normal (0,0,1), area 26.8mm2, adj f182
  f184: cylinder r=6.35mm len=15.24mm, axis (0,0,-1), area 101.3mm2, adj f0,f39,f40,f45
  f185: cylinder r=6.35mm len=15.24mm, axis (0,0,-1), area 101.3mm2, adj f0,f40,f41,f45
  f186: cylinder r=6.35mm len=15.24mm, axis (0,0,-1), area 101.3mm2, adj f0,f41,f42,f45
  f187: cylinder r=6.35mm len=15.24mm, axis (0,0,-1), area 101.3mm2, adj f0,f42,f43,f45
  f188: cylinder r=6.35mm len=15.24mm, axis (0,0,-1), area 101.3mm2, adj f0,f43,f44,f45
  f189: cylinder r=6.35mm len=15.24mm, axis (0,0,-1), area 101.3mm2, adj f0,f39,f44,f45
  f190: cone r=2.92mm half-angle=45deg, axis (0,0,1), area 49.9mm2, adj f0,f182
  f191: cone r=2.92mm half-angle=45deg, axis (0,0,1), area 49.9mm2, adj f0,f157
  f192: cone r=2.92mm half-angle=45deg, axis (0,0,1), area 49.9mm2, adj f0,f132
  f193: cone r=2.92mm half-angle=45deg, axis (0,0,1), area 49.9mm2, adj f0,f107
  f194: cone r=2.92mm half-angle=45deg, axis (0,0,1), area 49.9mm2, adj f0,f82
  f195: cone r=2.92mm half-angle=45deg, axis (0,0,1), area 49.9mm2, adj f0,f57
PLACE A rot(axis=(1,0,0),180deg) t=(-41.12,15.58,7.12)mm
PLACE B rot(axis=(0,1,0),180deg) t=(-22.16,34.63,-2.65)mm
PLACE C t=(-7,-3.21,-5.58)mm
PLACE D t=(180.64,34.63,-21.06)mm
MATE cylindrical B.f40 <-> D.f157  axis (0,0,1) through (123.34,40.03,-12.17)mm
MATE planar A.f0 <-> C.f4  axis (0,0,-1) through (44.22,1.87,3.94)mm
MATE planar B.f6 <-> D.f46  axis (0,0,-1) through (123.34,62.25,-5.82)mm
